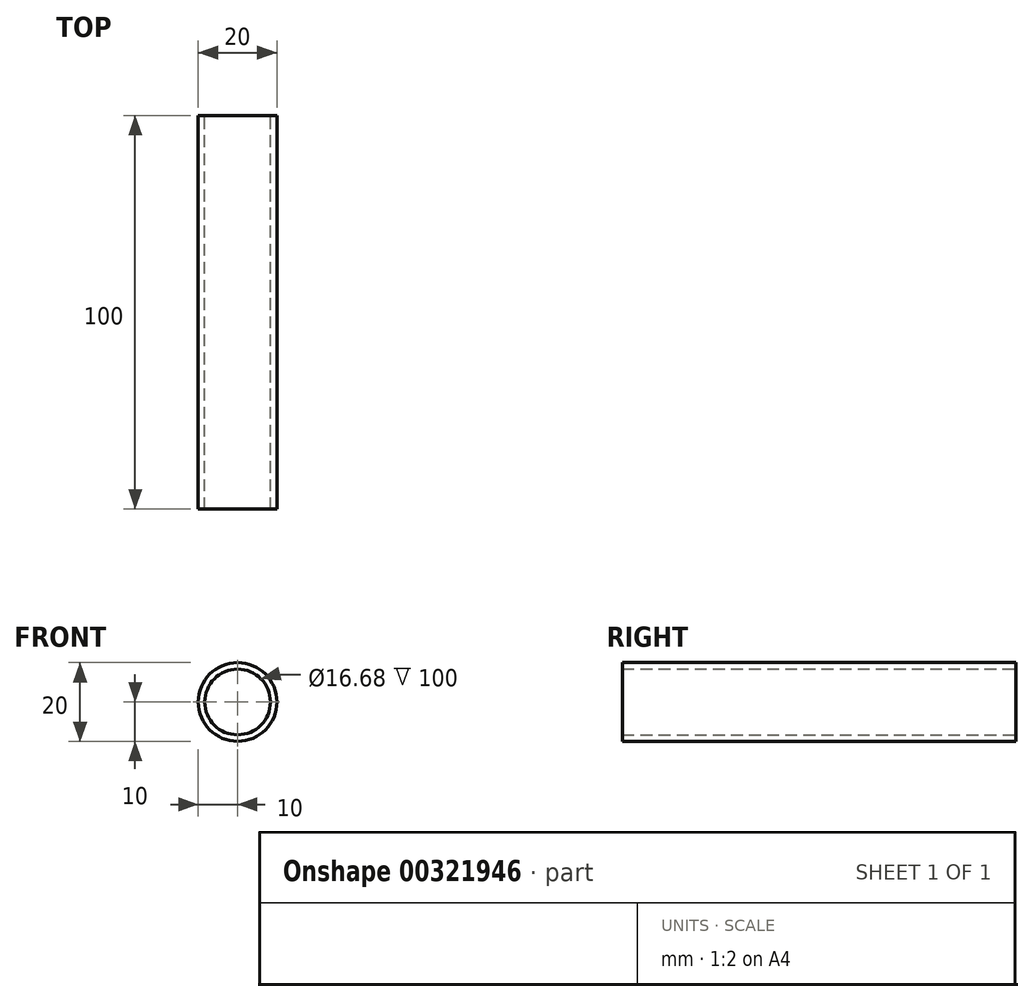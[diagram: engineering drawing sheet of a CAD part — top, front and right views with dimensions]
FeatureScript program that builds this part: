
annotation { "Feature Type Name" : "Feature", "Feature Type Description" : "" }
export const myFeature = defineFeature(function(context is Context, id is Id, definition is map)
    precondition{}
    {
        {
            var Q0;
            Q0=qCreatedBy(makeId("Front.planeOp"),FACE);
            var sketch = newSketch(context, id + "F0", { "sketchPlane" : qUnion([Q0])});
            skCircle(sketch, "E0", {"center": v(0, 0) * mm, "radius": 10 * mm});
            skSolve(sketch);
        }
        {
            var Q0;
            Q0=makeQuery(id+"F0.imprint","IMPRINT",FACE,{"disambiguationData":[TD([[makeQuery(id+"F0.imprint","IMPRINT",EDGE,{"derivedFrom":sQuery(id+"F0.wireOp",EDGE,"E0")}),1.0]])]});
            extrude(context, id + "F1", {"entities" : qUnion([Q0]), "depth" : 100 * mm});
        }
        {
            var Q0;
            Q0=qCreatedBy(makeId("Front.planeOp"),FACE);
            var sketch = newSketch(context, id + "F2", { "sketchPlane" : qUnion([Q0])});
            skCircle(sketch, "E1", {"center": v(0, 0) * mm, "radius": 8.5 * mm});
            skCircle(sketch, "E2.0", {"center": v(0, 0) * mm, "radius": 8.34 * mm});
            skSolve(sketch);
        }
        {
            var Q0;
            Q0=makeQuery(id+"F2.imprint","IMPRINT",FACE,{"disambiguationData":[TD([[makeQuery(id+"F2.imprint","IMPRINT",EDGE,{"derivedFrom":sQuery(id+"F2.wireOp",EDGE,"E2.0")}),1.0]])]});
            extrude(context, id + "F3", {"entities" : qUnion([Q0]), "operationType" : NewBodyOperationType.REMOVE, "depth" : 113.5 * mm});
        }
    });
